# Revit family: P500207-031
name_source: partatom
category: Lighting Fixtures
revit_build: Autodesk Revit 2014 (Build: 20130308_1515(x64)
units: mm (PartAtom-declared; Revit-internal decimal feet)

## types (1)
- P500207-031
    Apparent Load = 60 VA
    Assembly Code = D5020200
    Default Elevation = 48 "
    Description = Beautiful lighting will appeal to both your classic taste and your artistic spirit with the Bowman Collection Four-Light Black Pendant. Wandering eyes will focus on the clear, chiseled glass shade that encircles four elegant light sources gathering quietly at the light fixture's center. Handsome, black light bases with sophisticated curved arms originate from a decorative black knob that embellishes the outer bottom of the textured glass shade.
    Features = Wandering eyes will focus on the clear, chiseled glass shade that encircles the elegant light sources gathering quietly at the light fixture's center.
From the bottom of the sleek center column, a light base appears to gracefully drip down and provide an extra touch of refined visual interest.
Ideal for any foyer, dining room, or kitchen.
A sophisticated choice for luxury, modern, and transitional interiors.
Measures 14-1/4-inch width by 26-1/4-inch height.
Uses four candelabra base bulbs that are sold separately (60w max - LED or incandescent).
Able to be fully dimmable with dimmable bulbs.
Includes installation instructions and mounting hardware.
Progress Lighting products are designed for exceptional quality, reliability, and functionality.
    Fixture distribution = Direct
    Glass = Paint - Hubbell - White Texture
    Gold = Hubbell - Gold
    Height = 26.5 "
    Housing Material = Paint - Hubbell - Textured Camera Black
    Lamp = LED or Medium Base
    Load Classification = Lighting
    Manufacturer = Progress Lighting
    Model = P500207-031
    Power Factor = 1
    Product Documentation Link = https://hubbellcdn.com
    Product Link = https://www.hubbell.com
    Steel = Paint - Hubbell - Matte White
    URL = https://www.hubbell.com
    Voltage = 120 V
    Warranty = 1 year Warranty
    Wattage Comments = 60W
    Watts = 60 W
    Width = 6 "

## geometry (parser evidence)
native form markers: Sweep x6
no freeform markers — native parametric forms only
